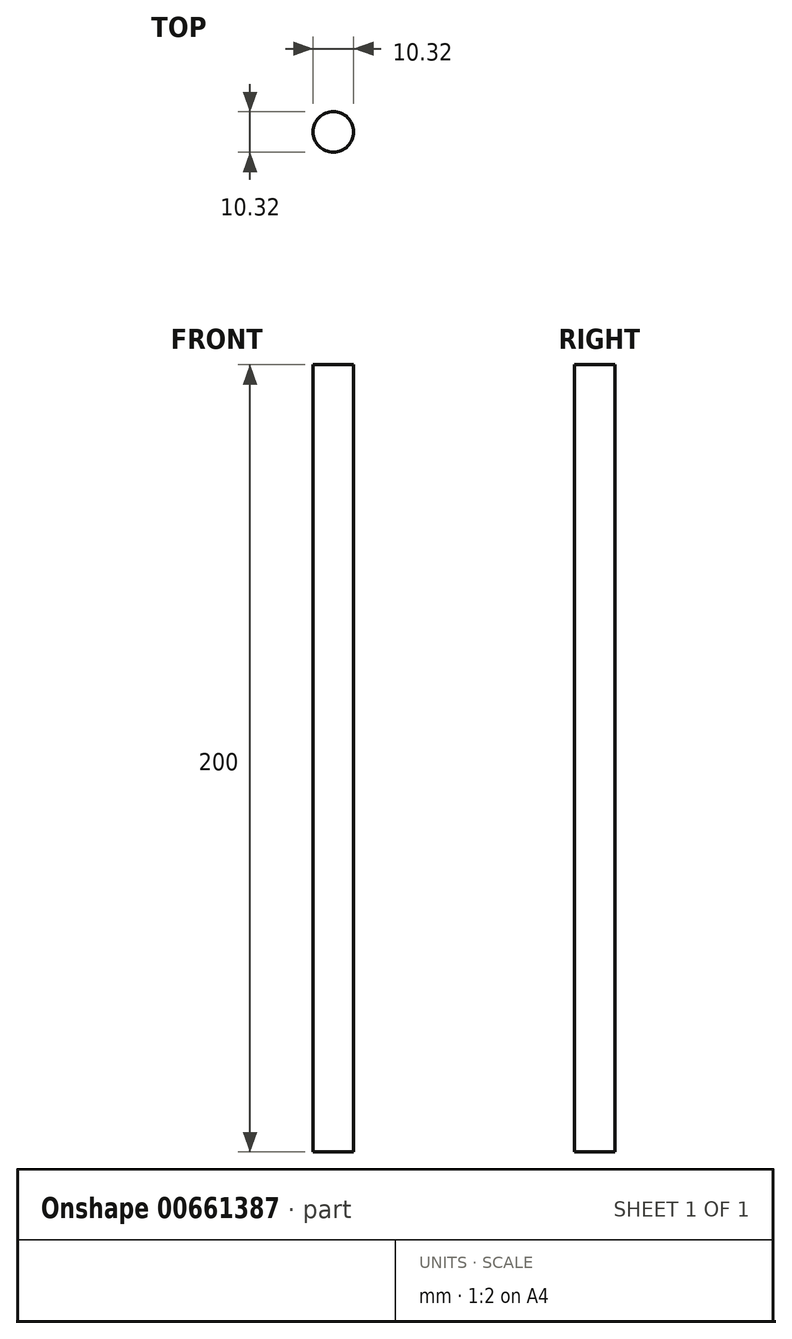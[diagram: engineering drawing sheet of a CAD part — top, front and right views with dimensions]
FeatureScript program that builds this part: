
annotation { "Feature Type Name" : "Feature", "Feature Type Description" : "" }
export const myFeature = defineFeature(function(context is Context, id is Id, definition is map)
    precondition{}
    {
        {
            var Q0;
            Q0=qCreatedBy(makeId("Top.planeOp"),FACE);
            var sketch = newSketch(context, id + "F0", { "sketchPlane" : qUnion([Q0])});
            skCircle(sketch, "E0", {"center": v(0, 0) * mm, "radius": 5.16 * mm});
            skSolve(sketch);
        }
        {
            var Q0;
            Q0=makeQuery(id+"F0.imprint","IMPRINT",FACE,{"disambiguationData":[TD([[makeQuery(id+"F0.imprint","IMPRINT",EDGE,{"derivedFrom":sQuery(id+"F0.wireOp",EDGE,"E0")}),1.0]])]});
            extrude(context, id + "F1", {"entities" : qUnion([Q0]), "oppositeDirection" : true, "depth" : 200 * mm, "offsetDistance" : 25 * mm});
        }
    });
